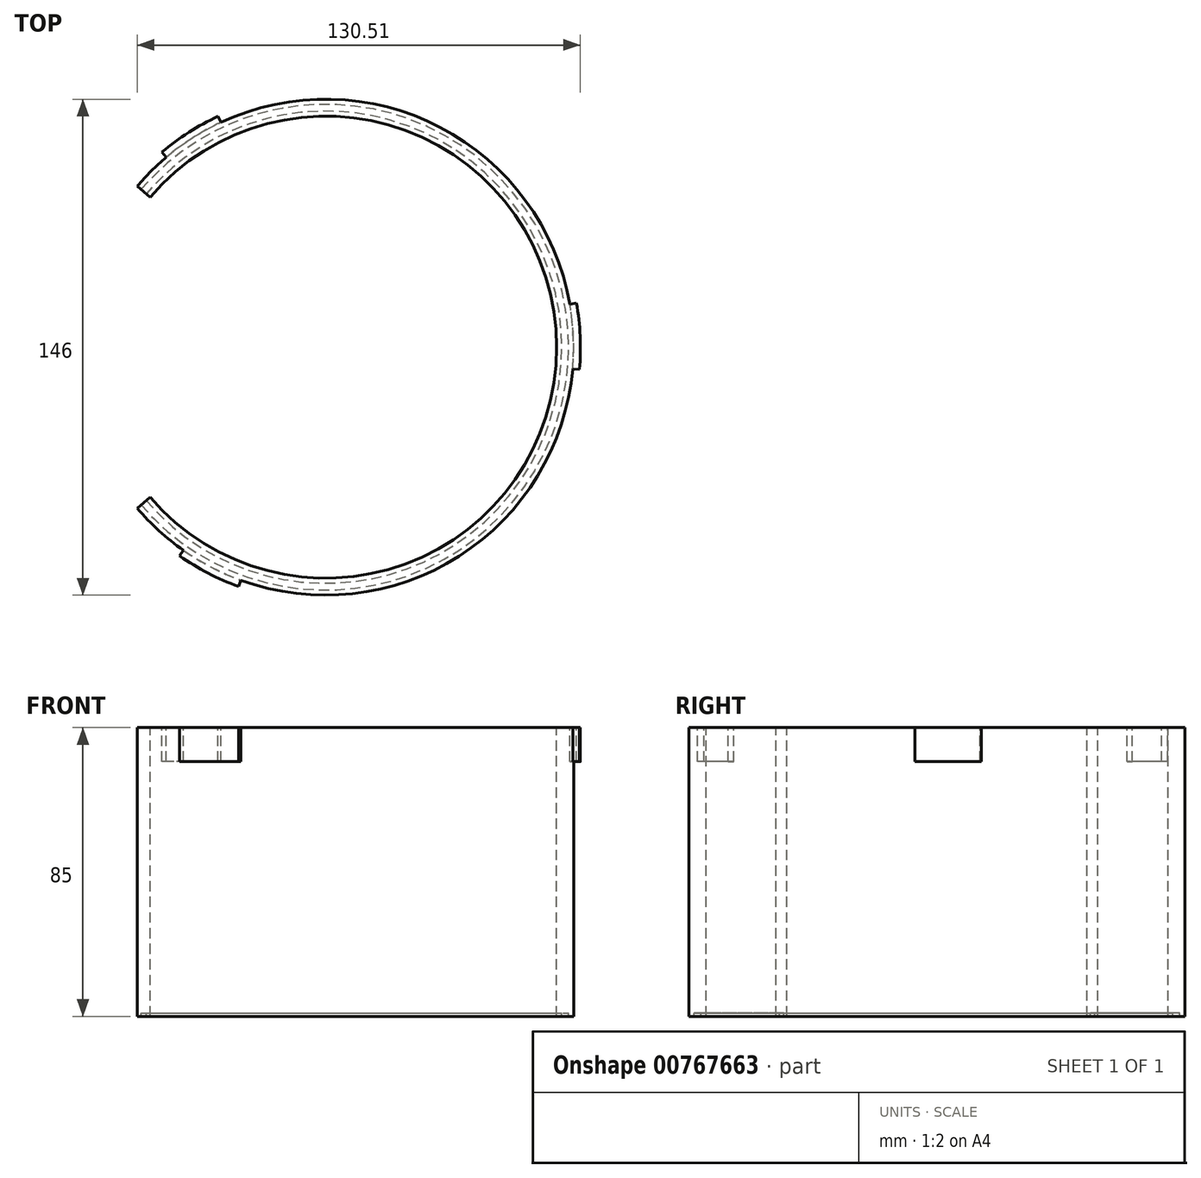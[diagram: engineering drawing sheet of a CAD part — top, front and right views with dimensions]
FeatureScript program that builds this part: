
annotation { "Feature Type Name" : "Feature", "Feature Type Description" : "" }
export const myFeature = defineFeature(function(context is Context, id is Id, definition is map)
    precondition{}
    {
        {
            var Q0;
            Q0=qCreatedBy(makeId("Front.planeOp"),FACE);
            var sketch = newSketch(context, id + "F0", { "sketchPlane" : qUnion([Q0])});
            skLineSegment(sketch, "E0", {"start": v(-73, 0) * mm, "end": v(-73, -85) * mm});
            skLineSegment(sketch, "E1", {"start": v(-68, -85) * mm, "end": v(-68, 0) * mm});
            skLineSegment(sketch, "E2", {"start": v(-68, 0) * mm, "end": v(-73, 0) * mm});
            skLineSegment(sketch, "E3", {"start": v(-73, -85) * mm, "end": v(-71.5, -85) * mm});
            skLineSegment(sketch, "E4", {"start": v(-71.5, -85) * mm, "end": v(-71.5, -84) * mm});
            skLineSegment(sketch, "E5", {"start": v(-71.5, -84) * mm, "end": v(-69.5, -84) * mm});
            skLineSegment(sketch, "E6", {"start": v(-69.5, -84) * mm, "end": v(-69.5, -85) * mm});
            skLineSegment(sketch, "E7", {"start": v(-69.5, -85) * mm, "end": v(-68, -85) * mm});
            skLineSegment(sketch, "E8", {"start": v(0, 0) * mm, "end": v(0, -24.91) * mm, "construction": true});
            skSolve(sketch);
        }
        {
            var Q0;
            Q0=makeQuery(id+"F0.imprint","IMPRINT",FACE,{"disambiguationData":[TD([[makeQuery(id+"F0.imprint","IMPRINT",EDGE,{"derivedFrom":sQuery(id+"F0.wireOp",EDGE,"E0")}),1.0]])]});
            var Q1;
            Q1=sQuery(id+"F0.wireOp",EDGE,"E8");
            revolve(context, id + "F1", {"surfaceOperationType" : NewSurfaceOperationType.NEW, "entities" : qUnion([Q0]), "axis" : qUnion([Q1]), "revolveType" : RevolveType.FULL});
        }
        {
            var Q0;
            Q0=makeQuery(id+"F1.opRevolve","SWEPT_FACE",FACE,{"disambiguationData":[OSD([sQuery(id+"F0.wireOp",EDGE,"E2")])]});
            var sketch = newSketch(context, id + "F2", { "sketchPlane" : qUnion([Q0])});
            skArc(sketch, "E9", {"start": v(-24.97, -68.6) * mm, "mid": v(-33.7, -64.75) * mm, "end": v(-41.87, -59.8) * mm});
            skArc(sketch, "E10", {"start": v(-43.02, -61.44) * mm, "mid": v(-34.63, -66.53) * mm, "end": v(-25.65, -70.48) * mm});
            skLineSegment(sketch, "E11", {"start": v(-24.97, -68.6) * mm, "end": v(-25.65, -70.48) * mm});
            skLineSegment(sketch, "E12", {"start": v(-43.02, -61.44) * mm, "end": v(-41.87, -59.8) * mm});
            skArc(sketch, "E13.1.0", {"start": v(71.9, 12.68) * mm, "mid": v(72.93, 3.18) * mm, "end": v(72.72, -6.36) * mm});
            skArc(sketch, "E13.1.1", {"start": v(74.71, -6.54) * mm, "mid": v(74.93, 3.27) * mm, "end": v(73.86, 13.02) * mm});
            skLineSegment(sketch, "E13.1.2", {"start": v(74.71, -6.54) * mm, "end": v(72.72, -6.36) * mm});
            skLineSegment(sketch, "E13.1.3", {"start": v(71.9, 12.68) * mm, "end": v(73.86, 13.02) * mm});
            skArc(sketch, "E13.2.0", {"start": v(-46.92, 55.92) * mm, "mid": v(-39.22, 61.57) * mm, "end": v(-30.85, 66.16) * mm});
            skArc(sketch, "E13.2.1", {"start": v(-31.7, 67.97) * mm, "mid": v(-40.3, 63.25) * mm, "end": v(-48.2, 57.45) * mm});
            skLineSegment(sketch, "E13.2.2", {"start": v(-31.7, 67.97) * mm, "end": v(-30.85, 66.16) * mm});
            skLineSegment(sketch, "E13.2.3", {"start": v(-46.92, 55.92) * mm, "end": v(-48.2, 57.45) * mm});
            skLineSegment(sketch, "E13.anchor1", {"start": v(0, 0) * mm, "end": v(-43.02, -61.44) * mm, "construction": true});
            skLineSegment(sketch, "E13.anchor2", {"start": v(0, 0) * mm, "end": v(-31.7, 67.97) * mm, "construction": true});
            skSolve(sketch);
        }
        {
            var Q0;
            Q0 = qSketchRegion(id + "F2", true);
            extrude(context, id + "F3", {"entities" : qUnion([Q0]), "operationType" : NewBodyOperationType.ADD, "oppositeDirection" : true, "depth" : 10 * mm, "offsetDistance" : 25 * mm});
        }
        {
            var Q0;
            Q0=makeQuery(id+"F3.boolean.opBoolean","MERGE",FACE,{"derivedFrom":[makeQuery(id+"F1.opRevolve","SWEPT_FACE",FACE,{"disambiguationData":[OSD([sQuery(id+"F0.wireOp",EDGE,"E2")])]}),makeQuery(id+"F3.opExtrude","CAP_FACE",FACE,{"disambiguationData":[OSD([sQuery(id+"F2.wireOp",EDGE,"E9"),sQuery(id+"F2.wireOp",EDGE,"E10"),sQuery(id+"F2.wireOp",EDGE,"E11"),sQuery(id+"F2.wireOp",EDGE,"E12")])],"isStart":true}),makeQuery(id+"F3.opExtrude","CAP_FACE",FACE,{"disambiguationData":[OSD([sQuery(id+"F2.wireOp",EDGE,"6ce37acd-3d40-4e89-9611-b017ba45b80d.1.0"),sQuery(id+"F2.wireOp",EDGE,"6ce37acd-3d40-4e89-9611-b017ba45b80d.1.1"),sQuery(id+"F2.wireOp",EDGE,"6ce37acd-3d40-4e89-9611-b017ba45b80d.1.2"),sQuery(id+"F2.wireOp",EDGE,"6ce37acd-3d40-4e89-9611-b017ba45b80d.1.3")])],"isStart":true}),makeQuery(id+"F3.opExtrude","CAP_FACE",FACE,{"disambiguationData":[OSD([sQuery(id+"F2.wireOp",EDGE,"6ce37acd-3d40-4e89-9611-b017ba45b80d.2.0"),sQuery(id+"F2.wireOp",EDGE,"6ce37acd-3d40-4e89-9611-b017ba45b80d.2.1"),sQuery(id+"F2.wireOp",EDGE,"6ce37acd-3d40-4e89-9611-b017ba45b80d.2.2"),sQuery(id+"F2.wireOp",EDGE,"6ce37acd-3d40-4e89-9611-b017ba45b80d.2.3")])],"isStart":true}),makeQuery(id+"F3.opExtrude","CAP_FACE",FACE,{"disambiguationData":[OSD([sQuery(id+"F2.wireOp",EDGE,"6ce37acd-3d40-4e89-9611-b017ba45b80d.3.0"),sQuery(id+"F2.wireOp",EDGE,"6ce37acd-3d40-4e89-9611-b017ba45b80d.3.1"),sQuery(id+"F2.wireOp",EDGE,"6ce37acd-3d40-4e89-9611-b017ba45b80d.3.2"),sQuery(id+"F2.wireOp",EDGE,"6ce37acd-3d40-4e89-9611-b017ba45b80d.3.3")])],"isStart":true})]});
            var sketch = newSketch(context, id + "F4", { "sketchPlane" : qUnion([Q0])});
            skArc(sketch, "E14", {"start": v(-55.5, -47.4) * mm, "mid": v(-73, 0) * mm, "end": v(-55.5, 47.4) * mm});
            skArc(sketch, "E15", {"start": v(-51.7, -44.16) * mm, "mid": v(-68, 0) * mm, "end": v(-51.7, 44.16) * mm});
            skLineSegment(sketch, "E16", {"start": v(-51.7, -44.16) * mm, "end": v(-55.5, -47.4) * mm});
            skLineSegment(sketch, "E17", {"start": v(-51.7, 44.16) * mm, "end": v(-55.5, 47.4) * mm});
            skSolve(sketch);
        }
        {
            var Q0;
            Q0 = qSketchRegion(id + "F4", true);
            var Q1;
            Q1=makeQuery(id+"F1.opRevolve","SWEPT_FACE",FACE,{"disambiguationData":[OSD([sQuery(id+"F0.wireOp",EDGE,"E3")])]});
            extrude(context, id + "F5", {"entities" : qUnion([Q0]), "operationType" : NewBodyOperationType.REMOVE, "endBound" : BoundingType.UP_TO_SURFACE, "oppositeDirection" : true, "depth" : 25 * mm, "endBoundEntityFace" : qUnion([Q1]), "offsetDistance" : 25 * mm});
        }
    });
